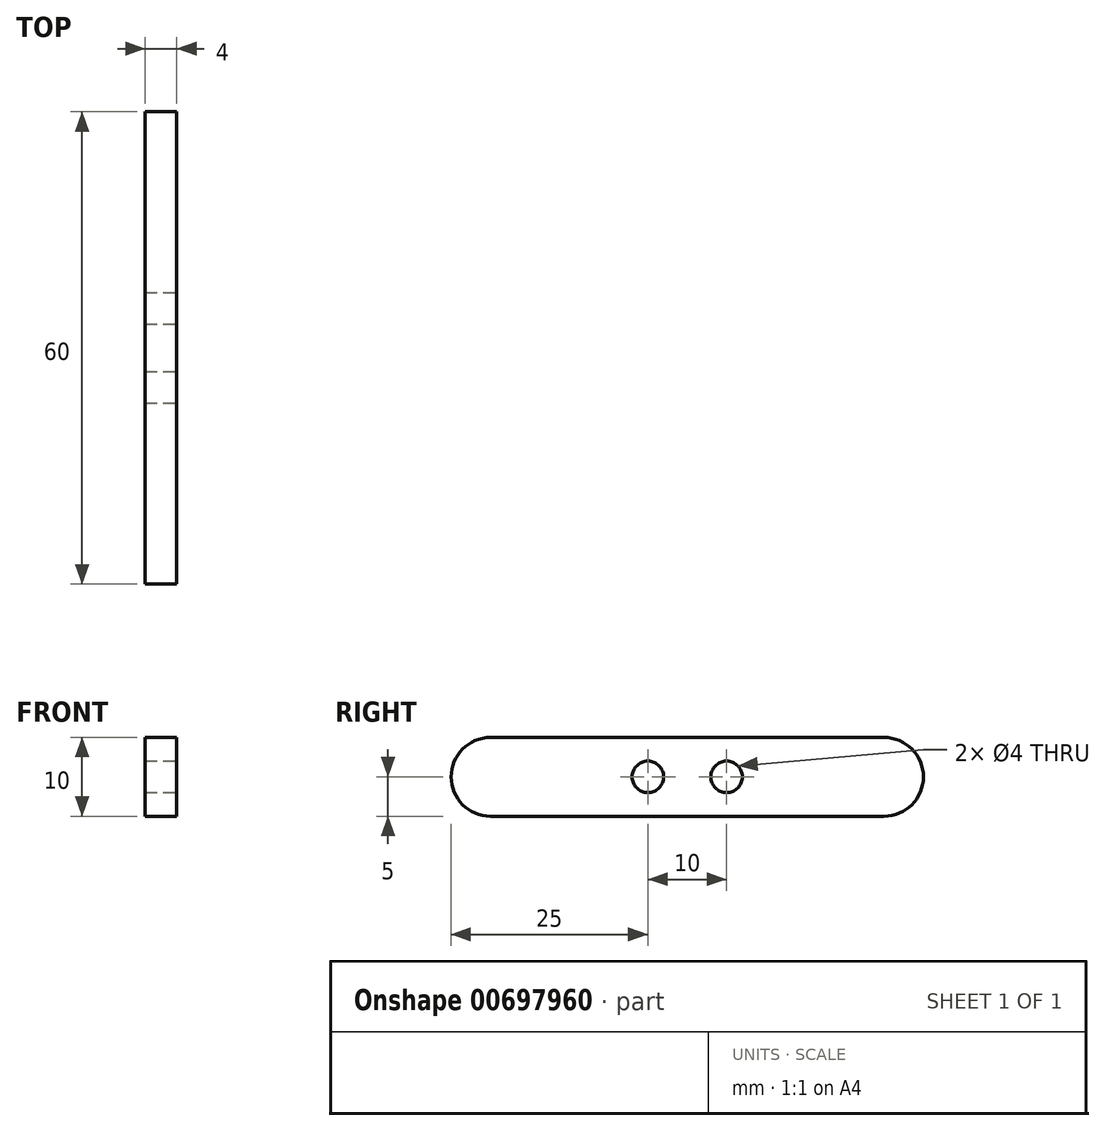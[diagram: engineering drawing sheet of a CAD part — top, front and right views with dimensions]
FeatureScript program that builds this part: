
annotation { "Feature Type Name" : "Feature", "Feature Type Description" : "" }
export const myFeature = defineFeature(function(context is Context, id is Id, definition is map)
    precondition{}
    {
        {
            var Q0;
            Q0=qCreatedBy(makeId("Right.planeOp"),FACE);
            var sketch = newSketch(context, id + "F0", { "sketchPlane" : qUnion([Q0])});
            skLineSegment(sketch, "E0.bottom", {"start": v(-32, 25.33) * mm, "end": v(18, 25.33) * mm});
            skLineSegment(sketch, "E0.top", {"start": v(-32, 15.33) * mm, "end": v(18, 15.33) * mm});
            skLineSegment(sketch, "E0.left", {"start": v(-37, 20.33) * mm, "end": v(-37, 20.33) * mm});
            skLineSegment(sketch, "E0.right", {"start": v(23, 20.33) * mm, "end": v(23, 20.33) * mm});
            skPoint(sketch, "E1.visualSharp", {"position": v(-37, 25.33) * mm});
            skArc(sketch, "E1.filletArc", {"start": v(-32, 25.33) * mm, "mid": v(-35.55, 23.87) * mm, "end": v(-37, 20.33) * mm});
            skPoint(sketch, "E2.visualSharp", {"position": v(-37, 15.33) * mm});
            skArc(sketch, "E2.filletArc", {"start": v(-37, 20.33) * mm, "mid": v(-35.55, 16.8) * mm, "end": v(-32, 15.33) * mm});
            skPoint(sketch, "E3.visualSharp", {"position": v(23, 25.33) * mm});
            skArc(sketch, "E3.filletArc", {"start": v(23, 20.33) * mm, "mid": v(21.53, 23.87) * mm, "end": v(18, 25.33) * mm});
            skPoint(sketch, "E4.visualSharp", {"position": v(23, 15.33) * mm});
            skArc(sketch, "E4.filletArc", {"start": v(18, 15.33) * mm, "mid": v(21.53, 16.8) * mm, "end": v(23, 20.33) * mm});
            skSolve(sketch);
        }
        {
            var Q0;
            Q0 = qSketchRegion(id + "F0", true);
            extrude(context, id + "F1", {"entities" : qUnion([Q0]), "depth" : 4 * mm, "offsetDistance" : 25 * mm});
        }
        {
            var Q0;
            Q0=makeQuery(id+"F1.opExtrude","CAP_FACE",FACE,{"disambiguationData":[OSD([sQuery(id+"F0.wireOp",EDGE,"E0.bottom"),sQuery(id+"F0.wireOp",EDGE,"E0.top"),sQuery(id+"F0.wireOp",EDGE,"E1.filletArc"),sQuery(id+"F0.wireOp",EDGE,"E2.filletArc"),sQuery(id+"F0.wireOp",EDGE,"E3.filletArc"),sQuery(id+"F0.wireOp",EDGE,"E4.filletArc")])],"isStart":false});
            var sketch = newSketch(context, id + "F2", { "sketchPlane" : qUnion([Q0])});
            skCircle(sketch, "E5", {"center": v(-12, 20.33) * mm, "radius": 2 * mm});
            skCircle(sketch, "E6", {"center": v(-2, 20.33) * mm, "radius": 2 * mm});
            skSolve(sketch);
        }
        {
            var Q0;
            Q0 = qSketchRegion(id + "F2", true);
            extrude(context, id + "F3", {"entities" : qUnion([Q0]), "operationType" : NewBodyOperationType.REMOVE, "oppositeDirection" : true, "depth" : 25 * mm, "offsetDistance" : 25 * mm});
        }
    });
